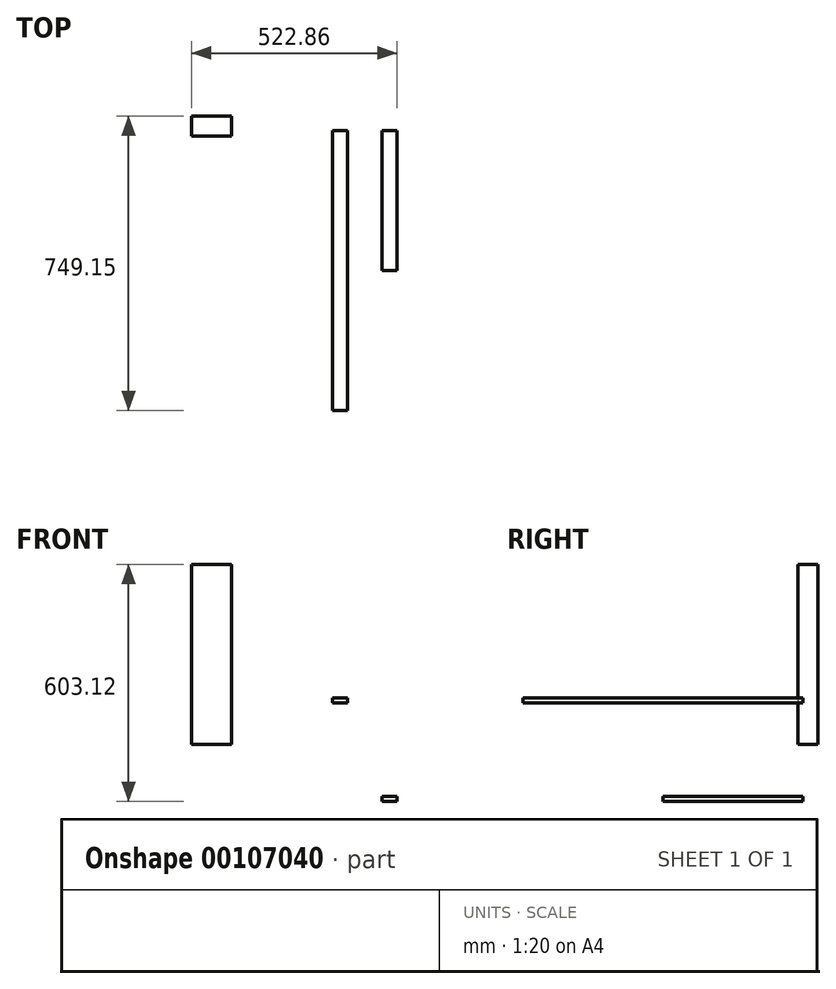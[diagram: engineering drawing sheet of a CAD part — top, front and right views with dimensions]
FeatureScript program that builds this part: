
annotation { "Feature Type Name" : "Feature", "Feature Type Description" : "" }
export const myFeature = defineFeature(function(context is Context, id is Id, definition is map)
    precondition{}
    {
        {
            var Q0;
            Q0=qCreatedBy(makeId("Top.planeOp"),FACE);
            var sketch = newSketch(context, id + "F0", { "sketchPlane" : qUnion([Q0])});
            skLineSegment(sketch, "E0.bottom", {"start": v(-101.6, 37.95) * mm, "end": v(0, 37.95) * mm});
            skLineSegment(sketch, "E0.top", {"start": v(-101.6, -12.85) * mm, "end": v(0, -12.85) * mm});
            skLineSegment(sketch, "E0.left", {"start": v(-101.6, 37.95) * mm, "end": v(-101.6, -12.85) * mm});
            skLineSegment(sketch, "E0.right", {"start": v(0, 37.95) * mm, "end": v(0, -12.85) * mm});
            skSolve(sketch);
        }
        {
            var Q0;
            Q0=makeQuery(id+"F0.imprint","IMPRINT",FACE,{"disambiguationData":[TD([[makeQuery(id+"F0.imprint","IMPRINT",EDGE,{"derivedFrom":sQuery(id+"F0.wireOp",EDGE,"E0.bottom")}),-1.0]])]});
            extrude(context, id + "F1", {"entities" : qUnion([Q0]), "depth" : 457.2 * mm});
        }
        {
            var Q0;
            Q0=qCreatedBy(makeId("Front.planeOp"),FACE);
            var sketch = newSketch(context, id + "F2", { "sketchPlane" : qUnion([Q0])});
            skLineSegment(sketch, "E1.bottom", {"start": v(383.16, -133.22) * mm, "end": v(421.26, -133.22) * mm});
            skLineSegment(sketch, "E1.top", {"start": v(383.16, -145.92) * mm, "end": v(421.26, -145.92) * mm});
            skLineSegment(sketch, "E1.left", {"start": v(383.16, -133.22) * mm, "end": v(383.16, -145.92) * mm});
            skLineSegment(sketch, "E1.right", {"start": v(421.26, -133.22) * mm, "end": v(421.26, -145.92) * mm});
            skSolve(sketch);
        }
        {
            var Q0;
            Q0=makeQuery(id+"F2.imprint","IMPRINT",FACE,{"disambiguationData":[TD([[makeQuery(id+"F2.imprint","IMPRINT",EDGE,{"derivedFrom":sQuery(id+"F2.wireOp",EDGE,"E1.bottom")}),-1.0]])]});
            extrude(context, id + "F3", {"entities" : qUnion([Q0]), "depth" : 355.6 * mm});
        }
        {
            var Q0;
            Q0=qCreatedBy(makeId("Front.planeOp"),FACE);
            var sketch = newSketch(context, id + "F4", { "sketchPlane" : qUnion([Q0])});
            skLineSegment(sketch, "E2.bottom", {"start": v(257.22, 117.83) * mm, "end": v(295.32, 117.83) * mm});
            skLineSegment(sketch, "E2.top", {"start": v(257.22, 105.13) * mm, "end": v(295.32, 105.13) * mm});
            skLineSegment(sketch, "E2.left", {"start": v(257.22, 117.83) * mm, "end": v(257.22, 105.13) * mm});
            skLineSegment(sketch, "E2.right", {"start": v(295.32, 117.83) * mm, "end": v(295.32, 105.13) * mm});
            skSolve(sketch);
        }
        {
            var Q0;
            Q0=makeQuery(id+"F4.imprint","IMPRINT",FACE,{"disambiguationData":[TD([[makeQuery(id+"F4.imprint","IMPRINT",EDGE,{"derivedFrom":sQuery(id+"F4.wireOp",EDGE,"E2.bottom")}),-1.0]])]});
            extrude(context, id + "F5", {"entities" : qUnion([Q0]), "depth" : 711.2 * mm});
        }
    });
